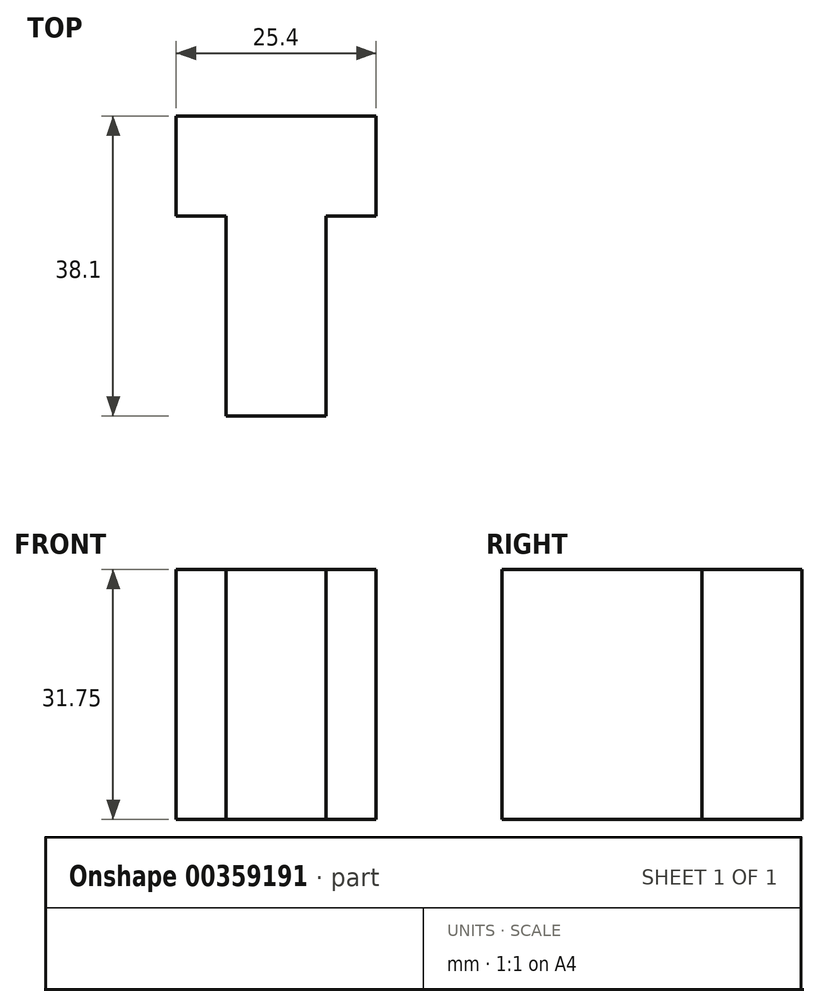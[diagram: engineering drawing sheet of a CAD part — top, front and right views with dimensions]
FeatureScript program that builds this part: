
annotation { "Feature Type Name" : "Feature", "Feature Type Description" : "" }
export const myFeature = defineFeature(function(context is Context, id is Id, definition is map)
    precondition{}
    {
        {
            var Q0;
            Q0=qCreatedBy(makeId("Top.planeOp"),FACE);
            var sketch = newSketch(context, id + "F0", { "sketchPlane" : qUnion([Q0])});
            skLineSegment(sketch, "E0", {"start": v(0, 0) * mm, "end": v(0, 25.4) * mm});
            skLineSegment(sketch, "E1", {"start": v(-6.35, 25.4) * mm, "end": v(-6.35, 38.1) * mm});
            skLineSegment(sketch, "E2", {"start": v(-6.35, 38.1) * mm, "end": v(19.05, 38.1) * mm});
            skLineSegment(sketch, "E3", {"start": v(19.05, 38.1) * mm, "end": v(19.05, 25.4) * mm});
            skLineSegment(sketch, "E4", {"start": v(19.05, 25.4) * mm, "end": v(12.7, 25.4) * mm});
            skLineSegment(sketch, "E5", {"start": v(12.7, 25.4) * mm, "end": v(12.7, 0) * mm});
            skLineSegment(sketch, "E6", {"start": v(12.7, 0) * mm, "end": v(0, 0) * mm});
            skLineSegment(sketch, "E7", {"start": v(-6.35, 25.4) * mm, "end": v(0, 25.4) * mm});
            skSolve(sketch);
        }
        {
            var Q0;
            Q0=qSketchRegion(id+"F0",true);
            extrude(context, id + "F1", {"entities" : qUnion([Q0]), "depth" : 31.75 * mm});
        }
    });
